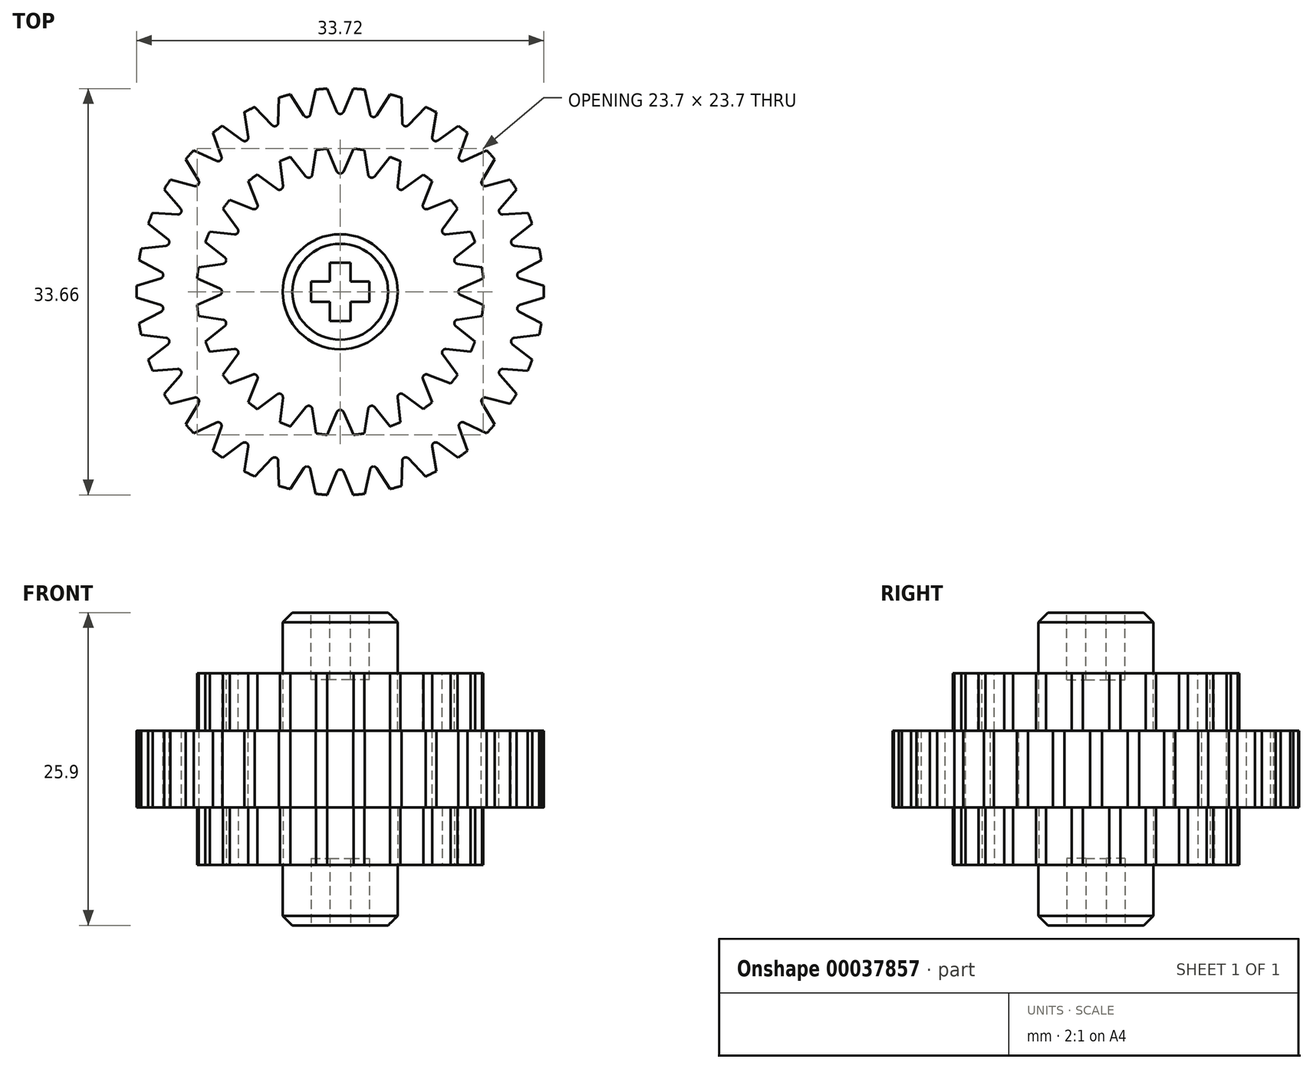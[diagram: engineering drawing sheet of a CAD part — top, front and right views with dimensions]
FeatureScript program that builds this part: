
annotation { "Feature Type Name" : "Feature", "Feature Type Description" : "" }
export const myFeature = defineFeature(function(context is Context, id is Id, definition is map)
    precondition{}
    {
        {
            var Q0;
            Q0=qCreatedBy(makeId("Top.planeOp"),FACE);
            var sketch = newSketch(context, id + "F0", { "sketchPlane" : qUnion([Q0])});
            skCircle(sketch, "E0", {"center": v(0, 0) * mm, "radius": 16.86 * mm});
            skSolve(sketch);
        }
        {
            var Q0;
            Q0=qSketchRegion(id+"F0",true);
            extrude(context, id + "F1", {"entities" : qUnion([Q0]), "endBound" : BoundingType.SYMMETRIC, "depth" : 6.35 * mm});
        }
        {
            var Q0;
            Q0=makeQuery(id+"F1.opExtrude","CAP_FACE",FACE,{"disambiguationData":[OSD([sQuery(id+"F0.wireOp",EDGE,"E0")])],"isStart":false});
            var sketch = newSketch(context, id + "F2", { "sketchPlane" : qUnion([Q0])});
            skLineSegment(sketch, "E1", {"start": v(0, 0) * mm, "end": v(0, 16.86) * mm, "construction": true});
            skArc(sketch, "E2", {"start": v(1.07, 16.83) * mm, "mid": v(0, 16.86) * mm, "end": v(-1.07, 16.83) * mm});
            skLineSegment(sketch, "E3", {"start": v(-1.07, 16.83) * mm, "end": v(-0.28, 14.91) * mm});
            skLineSegment(sketch, "E4", {"start": v(1.07, 16.83) * mm, "end": v(0.28, 14.91) * mm});
            skArc(sketch, "E5", {"start": v(-0.28, 14.91) * mm, "mid": v(0, 14.73) * mm, "end": v(0.28, 14.91) * mm});
            skLineSegment(sketch, "E6", {"start": v(0, 0) * mm, "end": v(-0.71, 16.85) * mm, "construction": true});
            skPoint(sketch, "E7", {"position": v(-0.67, 15.87) * mm});
            skSolve(sketch);
        }
        {
            var Q0;
            Q0=qSketchRegion(id+"F2",true);
            var Q1;
            Q1=makeQuery(id+"F1.opExtrude","CAP_FACE",FACE,{"disambiguationData":[OSD([sQuery(id+"F0.wireOp",EDGE,"E0")])],"isStart":true});
            extrude(context, id + "F3", {"entities" : qUnion([Q0]), "operationType" : NewBodyOperationType.REMOVE, "endBound" : BoundingType.UP_TO_SURFACE, "oppositeDirection" : true, "endBoundEntityFace" : qUnion([Q1]), "depth" : 25.4 * mm});
        }
        {
            var Q0;
            Q0=makeQuery(id+"F3.boolean.opBoolean","COPY",FACE,{"derivedFrom":makeQuery(id+"F3.opExtrude","SWEPT_FACE",FACE,{"disambiguationData":[OSD([sQuery(id+"F2.wireOp",EDGE,"E3")])]})});
            var Q1;
            Q1=makeQuery(id+"F3.boolean.opBoolean","COPY",FACE,{"derivedFrom":makeQuery(id+"F3.opExtrude","SWEPT_FACE",FACE,{"disambiguationData":[OSD([sQuery(id+"F2.wireOp",EDGE,"E5")])]})});
            var Q2;
            Q2=makeQuery(id+"F3.boolean.opBoolean","COPY",FACE,{"derivedFrom":makeQuery(id+"F3.opExtrude","SWEPT_FACE",FACE,{"disambiguationData":[OSD([sQuery(id+"F2.wireOp",EDGE,"E4")])]})});
            var Q3;
            Q3=makeQuery(id+"F1.opExtrude","SWEPT_FACE",FACE,{"disambiguationData":[OSD([sQuery(id+"F0.wireOp",EDGE,"E0")])]});
            circularPattern(context, id + "F4", {"faces" : qUnion([Q0, Q1, Q2]), "axis" : qUnion([Q3]), "angle" : 10.6 * degree, "instanceCount" : 34, "patternType" : PatternType.FACE});
        }
        {
            var Q0;
            Q0=qCreatedBy(makeId("Top.planeOp"),FACE);
            var sketch = newSketch(context, id + "F5", { "sketchPlane" : qUnion([Q0])});
            skCircle(sketch, "E8", {"center": v(0, 0) * mm, "radius": 4.76 * mm});
            skSolve(sketch);
        }
        {
            var Q0;
            Q0=qSketchRegion(id+"F5",true);
            extrude(context, id + "F6", {"entities" : qUnion([Q0]), "operationType" : NewBodyOperationType.ADD, "endBound" : BoundingType.SYMMETRIC, "depth" : 25.9 * mm});
        }
        {
            var Q0;
            Q0=makeQuery(id+"F6.opExtrude","CAP_EDGE",EDGE,{"disambiguationData":[OSD([sQuery(id+"F5.wireOp",EDGE,"E8")])],"isStart":false});
            var Q1;
            Q1=makeQuery(id+"F6.opExtrude","CAP_EDGE",EDGE,{"disambiguationData":[OSD([sQuery(id+"F5.wireOp",EDGE,"E8")])],"isStart":true});
            chamfer(context, id + "F7", {"entities" : qUnion([Q0, Q1]), "width" : 0.8 * mm, "tangentPropagation" : true});
        }
        {
            var Q0;
            Q0=qCreatedBy(makeId("Top.planeOp"),FACE);
            var sketch = newSketch(context, id + "F8", { "sketchPlane" : qUnion([Q0])});
            skCircle(sketch, "E9", {"center": v(0, 0) * mm, "radius": 11.9 * mm});
            skSolve(sketch);
        }
        {
            var Q0;
            Q0 = qSketchRegion(id + "F8", true);
            extrude(context, id + "F9", {"entities" : qUnion([Q0]), "operationType" : NewBodyOperationType.ADD, "endBound" : BoundingType.SYMMETRIC, "depth" : 15.88 * mm});
        }
        {
            var Q0;
            {var subQ0=sQuery(id+"F8.wireOp",EDGE,"E9");Q0=makeQuery(id+"F9.boolean.opBoolean","SPLIT",FACE,{"disambiguationData":[TD([makeQuery(id+"F6.opExtrude","SWEPT_FACE",FACE,{"disambiguationData":[OSD([sQuery(id+"F5.wireOp",EDGE,"E8")])]})])],"derivedFrom":makeQuery(id+"F9.opExtrude","CAP_FACE",FACE,{"disambiguationData":[OSD([subQ0])],"isStart":true})});}
            var sketch = newSketch(context, id + "F10", { "sketchPlane" : qUnion([Q0])});
            skLineSegment(sketch, "E10", {"start": v(0, 0) * mm, "end": v(0, -11.9) * mm, "construction": true});
            skArc(sketch, "E11", {"start": v(-1.1, -11.85) * mm, "mid": v(0, -11.9) * mm, "end": v(1.1, -11.85) * mm});
            skLineSegment(sketch, "E12", {"start": v(1.1, -11.85) * mm, "end": v(0.27, -9.97) * mm});
            skLineSegment(sketch, "E13", {"start": v(-1.1, -11.85) * mm, "end": v(-0.27, -9.97) * mm});
            skArc(sketch, "E14", {"start": v(0.27, -9.97) * mm, "mid": v(0, -9.79) * mm, "end": v(-0.27, -9.97) * mm});
            skPoint(sketch, "E15", {"position": v(0.68, -10.9) * mm});
            skLineSegment(sketch, "E16", {"start": v(0, 0) * mm, "end": v(0.74, -11.88) * mm, "construction": true});
            skSolve(sketch);
        }
        {
            var Q0;
            Q0 = qSketchRegion(id + "F10", true);
            var Q1;
            Q1=makeQuery(id+"F1.opExtrude","CAP_FACE",FACE,{"disambiguationData":[OSD([sQuery(id+"F0.wireOp",EDGE,"E0")])],"isStart":true});
            extrude(context, id + "F11", {"entities" : qUnion([Q0]), "operationType" : NewBodyOperationType.REMOVE, "endBound" : BoundingType.UP_TO_SURFACE, "oppositeDirection" : true, "endBoundEntityFace" : qUnion([Q1]), "depth" : 25.4 * mm});
        }
        {
            var Q0;
            {var subQ0=sQuery(id+"F8.wireOp",EDGE,"E9");Q0=makeQuery(id+"F9.boolean.opBoolean","SPLIT",FACE,{"disambiguationData":[TD([makeQuery(id+"F6.opExtrude","SWEPT_FACE",FACE,{"disambiguationData":[OSD([sQuery(id+"F5.wireOp",EDGE,"E8")])]})])],"derivedFrom":makeQuery(id+"F9.opExtrude","CAP_FACE",FACE,{"disambiguationData":[OSD([subQ0])],"isStart":false})});}
            var sketch = newSketch(context, id + "F12", { "sketchPlane" : qUnion([Q0])});
            skArc(sketch, "E17", {"start": v(1.1, 11.85) * mm, "mid": v(0, 11.9) * mm, "end": v(-1.1, 11.85) * mm});
            skLineSegment(sketch, "E18", {"start": v(-1.1, 11.85) * mm, "end": v(-0.27, 9.97) * mm});
            skLineSegment(sketch, "E19", {"start": v(1.1, 11.85) * mm, "end": v(0.27, 9.97) * mm});
            skArc(sketch, "E20", {"start": v(-0.27, 9.97) * mm, "mid": v(0, 9.79) * mm, "end": v(0.27, 9.97) * mm});
            skSolve(sketch);
        }
        {
            var Q0;
            Q0 = qSketchRegion(id + "F12", true);
            var Q1;
            Q1=makeQuery(id+"F1.opExtrude","CAP_FACE",FACE,{"disambiguationData":[OSD([sQuery(id+"F0.wireOp",EDGE,"E0")])],"isStart":false});
            extrude(context, id + "F13", {"entities" : qUnion([Q0]), "operationType" : NewBodyOperationType.REMOVE, "endBound" : BoundingType.UP_TO_SURFACE, "oppositeDirection" : true, "endBoundEntityFace" : qUnion([Q1]), "depth" : 25.4 * mm});
        }
        {
            var Q0;
            Q0=makeQuery(id+"F13.boolean.opBoolean","COPY",FACE,{"derivedFrom":makeQuery(id+"F13.opExtrude","SWEPT_FACE",FACE,{"disambiguationData":[OSD([sQuery(id+"F12.wireOp",EDGE,"E18")])]})});
            var Q1;
            Q1=makeQuery(id+"F13.boolean.opBoolean","COPY",FACE,{"derivedFrom":makeQuery(id+"F13.opExtrude","SWEPT_FACE",FACE,{"disambiguationData":[OSD([sQuery(id+"F12.wireOp",EDGE,"E20")])]})});
            var Q2;
            Q2=makeQuery(id+"F13.boolean.opBoolean","COPY",FACE,{"derivedFrom":makeQuery(id+"F13.opExtrude","SWEPT_FACE",FACE,{"disambiguationData":[OSD([sQuery(id+"F12.wireOp",EDGE,"E19")])]})});
            var Q3;
            Q3=makeQuery(id+"F11.boolean.opBoolean","COPY",FACE,{"derivedFrom":makeQuery(id+"F11.opExtrude","SWEPT_FACE",FACE,{"disambiguationData":[OSD([sQuery(id+"F10.wireOp",EDGE,"E12")])]})});
            var Q4;
            Q4=makeQuery(id+"F11.boolean.opBoolean","COPY",FACE,{"derivedFrom":makeQuery(id+"F11.opExtrude","SWEPT_FACE",FACE,{"disambiguationData":[OSD([sQuery(id+"F10.wireOp",EDGE,"E14")])]})});
            var Q5;
            Q5=makeQuery(id+"F11.boolean.opBoolean","COPY",FACE,{"derivedFrom":makeQuery(id+"F11.opExtrude","SWEPT_FACE",FACE,{"disambiguationData":[OSD([sQuery(id+"F10.wireOp",EDGE,"E13")])]})});
            var Q6;
            {var subQ0=sQuery(id+"F8.wireOp",EDGE,"E9");Q6=makeQuery(id+"F9.boolean.opBoolean","SPLIT",FACE,{"disambiguationData":[TD([makeQuery(id+"F1.opExtrude","CAP_FACE",FACE,{"disambiguationData":[OSD([sQuery(id+"F0.wireOp",EDGE,"E0")])],"isStart":true})])],"derivedFrom":makeQuery(id+"F9.opExtrude","SWEPT_FACE",FACE,{"disambiguationData":[OSD([subQ0])]})});}
            circularPattern(context, id + "F14", {"faces" : qUnion([Q0, Q1, Q2, Q3, Q4, Q5]), "axis" : qUnion([Q6]), "angle" : 15 * degree, "instanceCount" : 24, "patternType" : PatternType.FACE});
        }
        {
            var Q0;
            Q0=makeQuery(id+"F6.opExtrude","CAP_FACE",FACE,{"disambiguationData":[OSD([sQuery(id+"F5.wireOp",EDGE,"E8")])],"isStart":false});
            var sketch = newSketch(context, id + "F15", { "sketchPlane" : qUnion([Q0])});
            skLineSegment(sketch, "E21.rect.bottom", {"start": v(0.84, -2.41) * mm, "end": v(-0.84, -2.41) * mm});
            skLineSegment(sketch, "E21.rect.top", {"start": v(0.84, 2.41) * mm, "end": v(-0.84, 2.41) * mm});
            skLineSegment(sketch, "E21.rect.left", {"start": v(0.84, -2.41) * mm, "end": v(0.84, 2.41) * mm});
            skLineSegment(sketch, "E21.rect.right", {"start": v(-0.84, -2.41) * mm, "end": v(-0.84, 2.41) * mm});
            skPoint(sketch, "E21.rect.middle", {"position": v(0, 0) * mm});
            skLineSegment(sketch, "E22.rect.bottom", {"start": v(2.41, -0.84) * mm, "end": v(-2.41, -0.84) * mm});
            skLineSegment(sketch, "E22.rect.top", {"start": v(2.41, 0.84) * mm, "end": v(-2.41, 0.84) * mm});
            skLineSegment(sketch, "E22.rect.left", {"start": v(2.41, -0.84) * mm, "end": v(2.41, 0.84) * mm});
            skLineSegment(sketch, "E22.rect.right", {"start": v(-2.41, -0.84) * mm, "end": v(-2.41, 0.84) * mm});
            skSolve(sketch);
        }
        {
            var Q0;
            Q0 = qSketchRegion(id + "F15", true);
            extrude(context, id + "F16", {"entities" : qUnion([Q0]), "operationType" : NewBodyOperationType.REMOVE, "oppositeDirection" : true, "depth" : 5.56 * mm});
        }
        {
            var Q0;
            Q0=makeQuery(id+"F6.opExtrude","CAP_FACE",FACE,{"disambiguationData":[OSD([sQuery(id+"F5.wireOp",EDGE,"E8")])],"isStart":true});
            var sketch = newSketch(context, id + "F17", { "sketchPlane" : qUnion([Q0])});
            skLineSegment(sketch, "E23.rect.bottom", {"start": v(-0.84, -2.41) * mm, "end": v(0.84, -2.41) * mm});
            skLineSegment(sketch, "E23.rect.top", {"start": v(-0.84, 2.41) * mm, "end": v(0.84, 2.41) * mm});
            skLineSegment(sketch, "E23.rect.left", {"start": v(-0.84, -2.41) * mm, "end": v(-0.84, 2.41) * mm});
            skLineSegment(sketch, "E23.rect.right", {"start": v(0.84, -2.41) * mm, "end": v(0.84, 2.41) * mm});
            skPoint(sketch, "E23.rect.middle", {"position": v(0, 0) * mm});
            skLineSegment(sketch, "E24.rect.bottom", {"start": v(-2.41, 0.84) * mm, "end": v(2.41, 0.84) * mm});
            skLineSegment(sketch, "E24.rect.top", {"start": v(-2.41, -0.84) * mm, "end": v(2.41, -0.84) * mm});
            skLineSegment(sketch, "E24.rect.left", {"start": v(-2.41, 0.84) * mm, "end": v(-2.41, -0.84) * mm});
            skLineSegment(sketch, "E24.rect.right", {"start": v(2.41, 0.84) * mm, "end": v(2.41, -0.84) * mm});
            skSolve(sketch);
        }
        {
            var Q0;
            Q0 = qSketchRegion(id + "F17", true);
            extrude(context, id + "F18", {"entities" : qUnion([Q0]), "operationType" : NewBodyOperationType.REMOVE, "oppositeDirection" : true, "depth" : 5.56 * mm});
        }
    });
